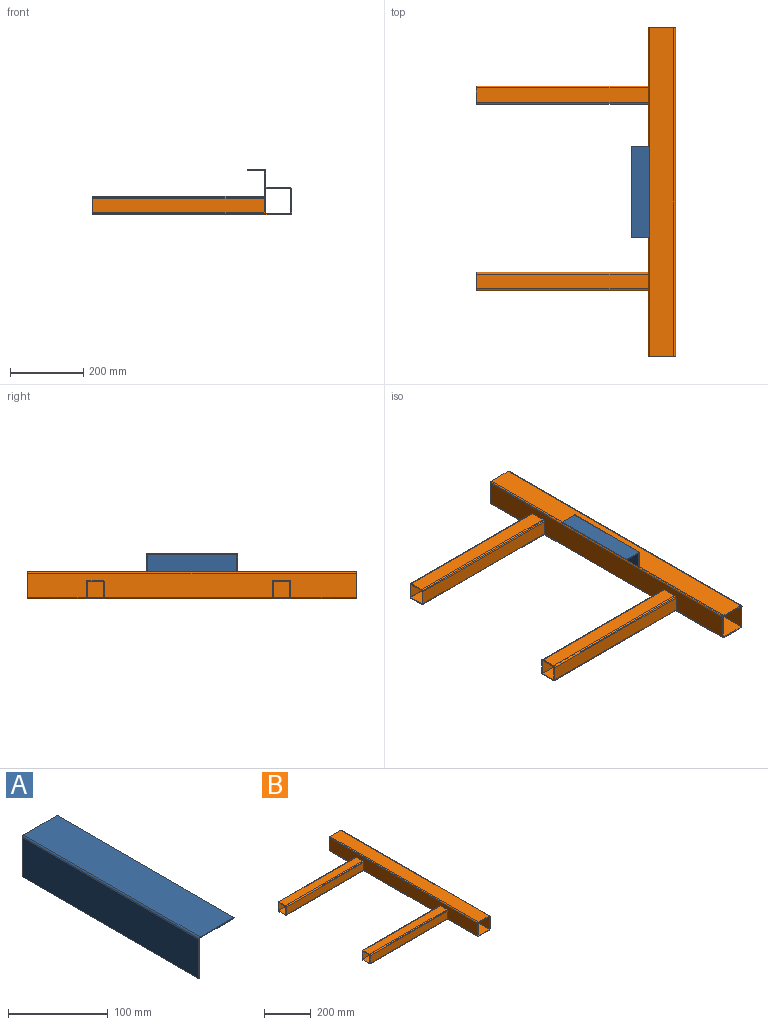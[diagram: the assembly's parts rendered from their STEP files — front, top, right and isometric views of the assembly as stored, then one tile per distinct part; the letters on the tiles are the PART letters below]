
ASSEMBLY  parts=2 mates=1
PART A: 11 faces, bbox 50x250x50 mm
  f0: plane 244x47mm, normal (0,0,-1), area 11468mm2, adj f1,f5,f8,f10
  f1: plane 250x3mm, normal (1,0,0), area 746.1mm2, adj f0,f2,f8,f10
  f2: plane 250x48mm, normal (0,0,1), area 12000mm2, adj f1,f6,f8,f10
  f3: plane 250x48mm, normal (-1,0,0), area 12000mm2, adj f4,f6,f7,f9
  f4: plane 250x3mm, normal (0,0,-1), area 746.1mm2, adj f3,f5,f7,f9
  f5: plane 244x47mm, normal (1,0,0), area 11468mm2, adj f0,f4,f7,f9
  f6: cylinder r=2mm len=250mm, axis (0,-1,0), area 785.3mm2, adj f2,f3,f7,f8,f9,f10
  f7: cylinder r=3mm len=49.41mm, axis (0,0,1), area 226.2mm2, adj f3,f4,f5,f6,f8
  f8: cylinder r=3mm len=49.41mm, axis (1,0,0), area 226.2mm2, adj f0,f1,f2,f6,f7
  f9: cylinder r=3mm len=49.41mm, axis (0,0,-1), area 226.2mm2, adj f3,f4,f5,f6,f10
  f10: cylinder r=3mm len=49.41mm, axis (-1,0,0), area 226.2mm2, adj f0,f1,f2,f6,f9
PART B: 42 faces, bbox 545x900x75 mm
  f0: plane 900x65mm, normal (-1,0,0), area 53921.6mm2, adj f8,f9,f11,f12,f17,f21,f22,f27
  f1: plane 900x65mm, normal (0,0,-1), area 58500mm2, adj f8,f9,f30,f33
  f2: plane 900x65mm, normal (1,0,0), area 58500mm2, adj f8,f9,f30,f31
  f3: plane 900x65mm, normal (0,0,1), area 58500mm2, adj f8,f9,f31,f32
  f4: plane 900x69mm, normal (-1,0,0), area 62100mm2, adj f5,f7,f8,f9
  f5: plane 900x69mm, normal (0,0,1), area 62100mm2, adj f4,f6,f8,f9
  f6: plane 900x69mm, normal (1,0,0), area 62100mm2, adj f5,f7,f8,f9
  f7: plane 900x69mm, normal (0,0,-1), area 62100mm2, adj f4,f6,f8,f9
  f8: plane 75x75mm, normal (0,-1,0), area 842.5mm2, adj f0,f1,f2,f3,f4,f5,f6,f7
  f9: plane 75x75mm, normal (0,1,0), area 842.5mm2, adj f0,f1,f2,f3,f4,f5,f6,f7
  f10: plane 472x40mm, normal (0,0,-1), area 18880mm2, adj f18,f33,f38,f41
  f11: plane 470x40mm, normal (0,-1,0), area 18800mm2, adj f0,f18,f38,f39
  f12: plane 470x40mm, normal (0,0,1), area 18800mm2, adj f0,f18,f39,f40
  f13: plane 470x44mm, normal (0,-1,0), area 20680mm2, adj f14,f16,f18,f19
  f14: plane 470x44mm, normal (0,0,-1), area 20680mm2, adj f13,f15,f18,f19
  f15: plane 470x44mm, normal (0,1,0), area 20680mm2, adj f14,f16,f18,f19
  f16: plane 470x44mm, normal (0,0,1), area 20680mm2, adj f13,f15,f18,f19
  f17: plane 470x40mm, normal (0,1,0), area 18800mm2, adj f0,f18,f40,f41
  f18: plane 50x50mm, normal (-1,0,0), area 542.5mm2, adj f10,f11,f12,f13,f14,f15,f16,f17
  f19: plane 44x44mm, normal (-1,0,0), area 1936mm2, adj f13,f14,f15,f16
  f20: plane 472x40mm, normal (0,0,-1), area 18880mm2, adj f28,f33,f34,f37
  f21: plane 470x40mm, normal (0,-1,0), area 18800mm2, adj f0,f28,f34,f35
  f22: plane 470x40mm, normal (0,0,1), area 18800mm2, adj f0,f28,f35,f36
  f23: plane 470x44mm, normal (0,-1,0), area 20680mm2, adj f24,f26,f28,f29
  f24: plane 470x44mm, normal (0,0,-1), area 20680mm2, adj f23,f25,f28,f29
  f25: plane 470x44mm, normal (0,1,0), area 20680mm2, adj f24,f26,f28,f29
  f26: plane 470x44mm, normal (0,0,1), area 20680mm2, adj f23,f25,f28,f29
  f27: plane 470x40mm, normal (0,1,0), area 18800mm2, adj f0,f28,f36,f37
  f28: plane 50x50mm, normal (-1,0,0), area 542.5mm2, adj f20,f21,f22,f23,f24,f25,f26,f27
  f29: plane 44x44mm, normal (-1,0,0), area 1936mm2, adj f23,f24,f25,f26
  f30: cylinder r=5mm len=900mm, axis (0,-1,0), area 7068.6mm2, adj f1,f2,f8,f9
  f31: cylinder r=5mm len=900mm, axis (0,1,0), area 7068.6mm2, adj f2,f3,f8,f9
  f32: cylinder r=5mm len=900mm, axis (0,-1,0), area 7068.6mm2, adj f0,f3,f8,f9
  f33: cylinder r=5mm len=900mm, axis (0,1,0), area 6632.7mm2, adj f0,f1,f8,f9,f10,f20,f34,f37
  f34: cylinder r=5mm len=472mm, axis (-1,0,0), area 3697.9mm2, adj f0,f20,f21,f28,f33
  f35: cylinder r=5mm len=470mm, axis (1,0,0), area 3691.4mm2, adj f0,f21,f22,f28
  f36: cylinder r=5mm len=470mm, axis (-1,0,0), area 3691.4mm2, adj f0,f22,f27,f28
  f37: cylinder r=5mm len=472mm, axis (1,0,0), area 3697.9mm2, adj f0,f20,f27,f28,f33
  f38: cylinder r=5mm len=472mm, axis (-1,0,0), area 3697.9mm2, adj f0,f10,f11,f18,f33
  f39: cylinder r=5mm len=470mm, axis (1,0,0), area 3691.4mm2, adj f0,f11,f12,f18
  f40: cylinder r=5mm len=470mm, axis (-1,0,0), area 3691.4mm2, adj f0,f12,f17,f18
  f41: cylinder r=5mm len=472mm, axis (1,0,0), area 3697.9mm2, adj f0,f10,f17,f18,f33
PLACE A rot(axis=(0,1,0),90deg) t=(62.19,295.52,-55.92)mm
PLACE B t=(120.2,620.52,-118.42)mm
MATE planar B.f3 <-> A.f1  axis (0,0,1) through (120.2,170.52,-80.92)mm
